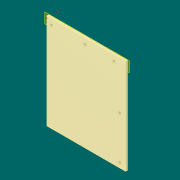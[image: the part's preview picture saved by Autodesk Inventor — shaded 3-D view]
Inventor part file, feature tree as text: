
AUTODESK INVENTOR PART (.ipt)
format: ipt  version: 2019 (Build 230136000, 136)  size: 188,416 bytes
history: native  units: mm
features: sketch x14, reference x13, extrude x10, other x3, plane x1
ambient origin geometry x8: Origin, YZ Plane, XZ Plane, XY Plane, X Axis, Y Axis, Z Axis, Center Point
bodies: Solid1 (feature_tree)
feature tree (41):
  plane  "Work Plane1"
  extrude  "Extrusion1"  Depth=2.0mm
  extrude  "Extrusion2"  Depth=2.5mm
  extrude  "Extrusion3"  Depth=2.5mm
  extrude  "Extrusion4"  Depth=8.0mm
  extrude  "Extrusion5"  Depth=8.0mm
  sketch  "Sketch6"  dims[d13=1.5mm d14=5.0mm d15=0.0mm]
  sketch  "Sketch7"  dims[d16=8.0mm d17=10.0mm]
  extrude  "Extrusion6"  Depth=5.0mm TaperAngle=0.0deg
  extrude  "Extrusion7"  Depth=10.0mm
  extrude  "Extrusion8"  Depth=5.0mm TaperAngle=0.0deg
  extrude  "Extrusion9"  Depth=8.0mm
  sketch  "Sketch12"  dims[d30=8.0mm d31=0.0mm]
  sketch  "Sketch13"  dims[d33=10.0mm]
  extrude  "Extrusion10"  Depth=1.5mm
  sketch  "Sketch1"  dims[d0=2.0mm d1=0.0mm d2=2.5mm]
  reference  "Reference1"
  reference  "Reference2"
  reference  "Reference3"
  reference  "Reference4"
  reference  "Reference5"
  reference  "Reference6"
  reference  "Reference7"
  reference  "Reference8"
  reference  "Reference9"
  sketch  "Sketch2"  dims[d3=2.5mm d4=2.5mm]
  sketch  "Sketch3"  dims[d5=2.5mm d6=2.5mm]
  reference  "Reference10"
  reference  "Reference11"
  sketch  "Sketch4"  dims[d7=2.0mm d8=0.0mm d9=8.0mm]
  sketch  "Sketch5"  dims[d10=10.0mm d11=8.0mm]
  reference  "Reference12"
  reference  "Reference13"
  sketch  "Sketch8"  dims[d19=1.5mm d20=5.0mm d21=0.0mm]
  sketch  "Sketch9"  dims[d22=10.0mm d23=8.0mm]
  sketch  "Sketch10"  dims[d25=1.5mm d27=1.5mm]
  sketch  "Sketch11"  dims[d28=5.0mm d29=0.0mm]
  sketch  "Sketch14"  dims[d34=8.0mm d35=10.0mm d38=8.0mm d39=0.0mm d40=8.0mm d41=0.0mm d42=15.0mm d43=8.0mm d44=10.0mm d45=8.0mm d46=0.0mm d50=1.5mm d51=8.0mm d52=0.0mm]
  other  "Ensamblaje Reloj LCD 16x2.iam"
  other  "Down:1"
  other  "Before:1"
